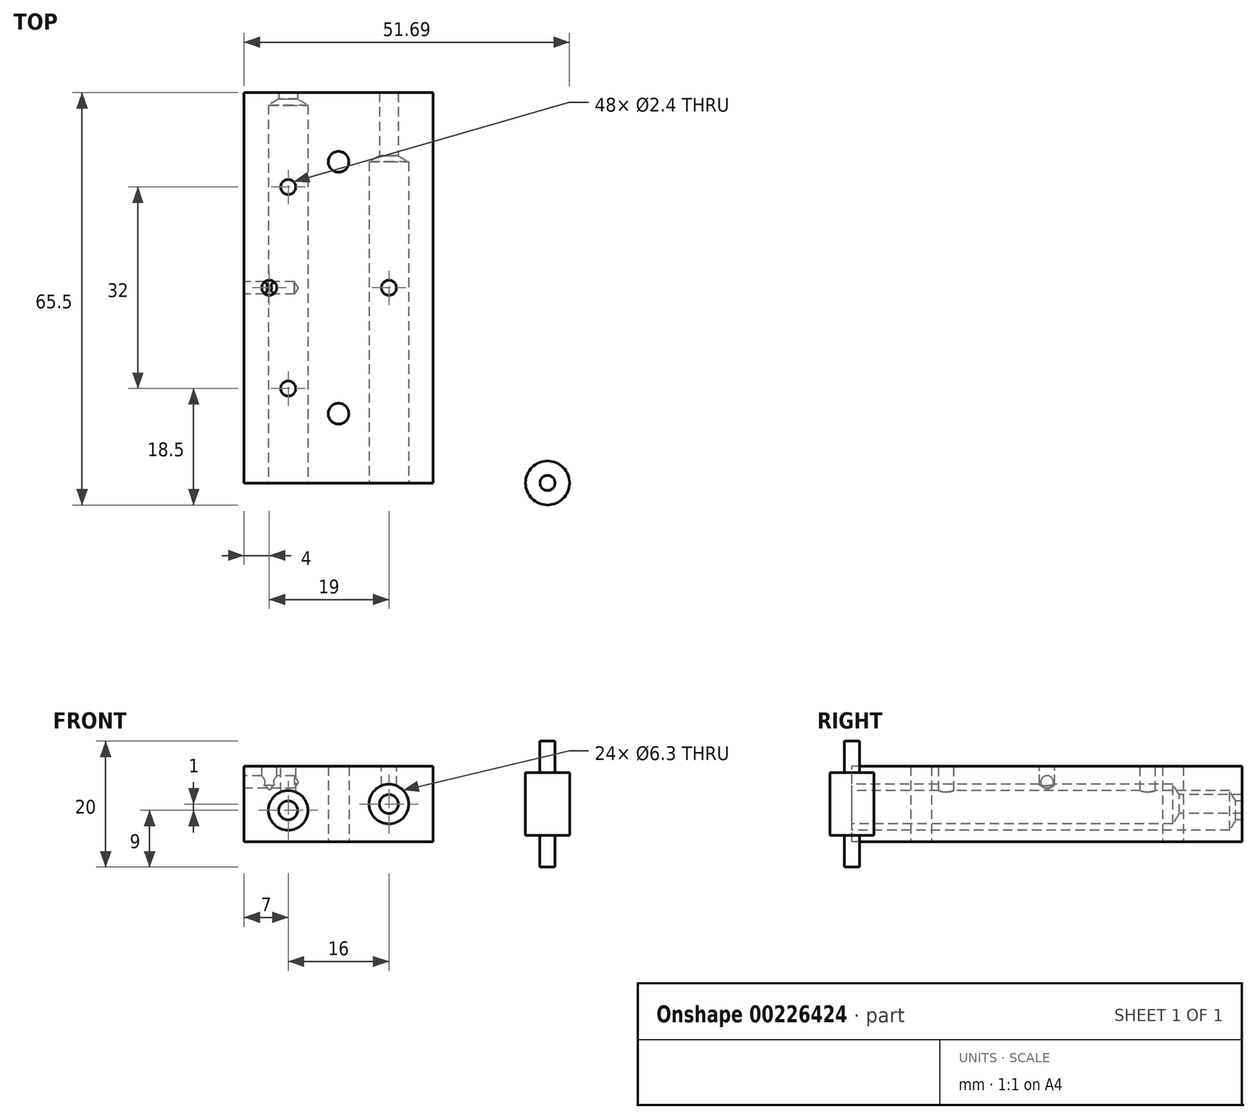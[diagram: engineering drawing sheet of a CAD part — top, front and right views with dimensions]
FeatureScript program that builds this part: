
annotation { "Feature Type Name" : "Feature", "Feature Type Description" : "" }
export const myFeature = defineFeature(function(context is Context, id is Id, definition is map)
    precondition{}
    {
        {
            var Q0;
            Q0=qCreatedBy(makeId("Front.planeOp"),FACE);
            var sketch = newSketch(context, id + "F0", { "sketchPlane" : qUnion([Q0])});
            skLineSegment(sketch, "E0.bottom", {"start": v(15, -6) * mm, "end": v(-15, -6) * mm});
            skLineSegment(sketch, "E0.top", {"start": v(15, 6) * mm, "end": v(-15, 6) * mm});
            skLineSegment(sketch, "E0.left", {"start": v(15, -6) * mm, "end": v(15, 6) * mm});
            skLineSegment(sketch, "E0.right", {"start": v(-15, -6) * mm, "end": v(-15, 6) * mm});
            skPoint(sketch, "E0.middle", {"position": v(0, 0) * mm});
            skPoint(sketch, "E1", {"position": v(-8, -1) * mm});
            skPoint(sketch, "E2", {"position": v(8, 0) * mm});
            skSolve(sketch);
        }
        {
            var Q0;
            Q0=makeQuery(id+"F0.imprint","IMPRINT",FACE,{"disambiguationData":[TD([[makeQuery(id+"F0.imprint","IMPRINT",EDGE,{"derivedFrom":sQuery(id+"F0.wireOp",EDGE,"E0.bottom")}),-1.0]])]});
            extrude(context, id + "F1", {"entities" : qUnion([Q0]), "oppositeDirection" : true, "depth" : 62 * mm});
        }
        {
            var Q0;
            Q0=sQuery(id+"F0.wireOp",VERTEX,"E1");
            var Q1;
            Q1=makeQuery(id+"F1.opExtrude","SWEPT_BODY",BODY,{"disambiguationData":[OSD([sQuery(id+"F0.wireOp",EDGE,"E0.bottom"),sQuery(id+"F0.wireOp",EDGE,"E0.top"),sQuery(id+"F0.wireOp",EDGE,"E0.left"),sQuery(id+"F0.wireOp",EDGE,"E0.right")])]});
            hole(context, id + "F2", {"style" : HoleStyle.SIMPLE, "endStyle" : HoleEndStyle.BLIND, "holeDiameter" : 6.3 * mm, "holeDepth" : 60 * mm, "startFromSketch" : true, "locations" : qUnion([Q0]), "scope" : qUnion([Q1])});
        }
        {
            var Q0;
            Q0=sQuery(id+"F0.wireOp",VERTEX,"E2");
            var Q1;
            Q1=makeQuery(id+"F1.opExtrude","SWEPT_BODY",BODY,{"disambiguationData":[OSD([sQuery(id+"F0.wireOp",EDGE,"E0.bottom"),sQuery(id+"F0.wireOp",EDGE,"E0.top"),sQuery(id+"F0.wireOp",EDGE,"E0.left"),sQuery(id+"F0.wireOp",EDGE,"E0.right")])]});
            hole(context, id + "F3", {"style" : HoleStyle.SIMPLE, "endStyle" : HoleEndStyle.BLIND, "holeDiameter" : 6.3 * mm, "holeDepth" : 51 * mm, "startFromSketch" : true, "locations" : qUnion([Q0]), "scope" : qUnion([Q1])});
        }
        {
            var Q0;
            Q0=makeQuery(id+"F1.opExtrude","SWEPT_FACE",FACE,{"disambiguationData":[OSD([sQuery(id+"F0.wireOp",EDGE,"E0.bottom")])]});
            var sketch = newSketch(context, id + "F4", { "sketchPlane" : qUnion([Q0])});
            skPoint(sketch, "E3", {"position": v(0, -11) * mm});
            skPoint(sketch, "E4", {"position": v(0, -51) * mm});
            skSolve(sketch);
        }
        {
            var Q0;
            Q0=sQuery(id+"F4.wireOp",VERTEX,"E3");
            var Q1;
            Q1=sQuery(id+"F4.wireOp",VERTEX,"E4");
            var Q2;
            Q2=makeQuery(id+"F1.opExtrude","SWEPT_BODY",BODY,{"disambiguationData":[OSD([sQuery(id+"F0.wireOp",EDGE,"E0.bottom"),sQuery(id+"F0.wireOp",EDGE,"E0.top"),sQuery(id+"F0.wireOp",EDGE,"E0.left"),sQuery(id+"F0.wireOp",EDGE,"E0.right")])]});
            hole(context, id + "F5", {"style" : HoleStyle.SIMPLE, "endStyle" : HoleEndStyle.THROUGH, "standardTappedOrClearance" : lookupTablePath({ "standard" : "ISO", "fit" : "Normal", "size" : "M3", "type" : "Clearance" }), "standardBlindInLast" : lookupTablePath({ "fit" : "Standard", "standard" : "ISO", "size" : "M3", "type" : "Clearance" }), "holeDiameter" : 3.3 * mm, "locations" : qUnion([Q0, Q1]), "scope" : qUnion([Q2]), "isTappedThrough" : true});
        }
        {
            var Q0;
            Q0=qCreatedBy(makeId("Top.planeOp"),FACE);
            var sketch = newSketch(context, id + "F6", { "sketchPlane" : qUnion([Q0])});
            skCircle(sketch, "E5", {"center": v(33.2, 0) * mm, "radius": 1.2 * mm});
            skCircle(sketch, "E6", {"center": v(33.2, 0) * mm, "radius": 3.5 * mm});
            skSolve(sketch);
        }
        {
            var Q0;
            Q0=makeQuery(id+"F6.imprint","IMPRINT",FACE,{"disambiguationData":[TD([[makeQuery(id+"F6.imprint","IMPRINT",EDGE,{"derivedFrom":sQuery(id+"F6.wireOp",EDGE,"E5")}),1.0]])]});
            var Q1;
            Q1=sQuery(id+"F6.wireOp",EDGE,"E5");
            extrude(context, id + "F7", {"entities" : qUnion([Q0]), "surfaceEntities" : qUnion([Q1]), "endBound" : BoundingType.SYMMETRIC, "depth" : 20 * mm});
        }
        {
            var Q0;
            Q0 = qSketchRegion(id + "F6", true);
            var Q1;
            Q1 = qSketchRegion(id + "FU8VzBIHLZZ5y2s_1", true);
            extrude(context, id + "F8", {"entities" : qUnion([Q0, Q1]), "operationType" : NewBodyOperationType.ADD, "endBound" : BoundingType.SYMMETRIC, "depth" : 10 * mm});
        }
        {
            var Q0;
            Q0=makeQuery(id+"F1.opExtrude","SWEPT_FACE",FACE,{"disambiguationData":[OSD([sQuery(id+"F0.wireOp",EDGE,"E0.right")])]});
            var sketch = newSketch(context, id + "F9", { "sketchPlane" : qUnion([Q0])});
            skPoint(sketch, "E7", {"position": v(-31, 3.5) * mm});
            skSolve(sketch);
        }
        {
            var Q0;
            Q0=sQuery(id+"F9.wireOp",VERTEX,"E7");
            var Q1;
            Q1=makeQuery(id+"F1.opExtrude","SWEPT_BODY",BODY,{"disambiguationData":[OSD([sQuery(id+"F0.wireOp",EDGE,"E0.bottom"),sQuery(id+"F0.wireOp",EDGE,"E0.top"),sQuery(id+"F0.wireOp",EDGE,"E0.left"),sQuery(id+"F0.wireOp",EDGE,"E0.right")])]});
            hole(context, id + "F10", {"style" : HoleStyle.SIMPLE, "endStyle" : HoleEndStyle.BLIND, "holeDiameter" : 2 * mm, "holeDepth" : 8 * mm, "startFromSketch" : true, "locations" : qUnion([Q0]), "scope" : qUnion([Q1])});
        }
        {
            var Q0;
            Q0=makeQuery(id+"F1.opExtrude","SWEPT_FACE",FACE,{"disambiguationData":[OSD([sQuery(id+"F0.wireOp",EDGE,"E0.top")])]});
            var sketch = newSketch(context, id + "F11", { "sketchPlane" : qUnion([Q0])});
            skPoint(sketch, "E8", {"position": v(-8, 15) * mm});
            skPoint(sketch, "E9", {"position": v(-11, 31) * mm});
            skPoint(sketch, "E9.positionSnap0", {"position": v(-15, 31) * mm});
            skPoint(sketch, "E10", {"position": v(8, 31) * mm});
            skPoint(sketch, "E11", {"position": v(-8, 47) * mm});
            skSolve(sketch);
        }
        {
            var Q0;
            Q0=sQuery(id+"F11.wireOp",VERTEX,"E8");
            var Q1;
            Q1=sQuery(id+"F11.wireOp",VERTEX,"E11");
            var Q2;
            Q2=sQuery(id+"F11.wireOp",VERTEX,"E10");
            var Q3;
            Q3=makeQuery(id+"F1.opExtrude","SWEPT_BODY",BODY,{"disambiguationData":[OSD([sQuery(id+"F0.wireOp",EDGE,"E0.bottom"),sQuery(id+"F0.wireOp",EDGE,"E0.top"),sQuery(id+"F0.wireOp",EDGE,"E0.left"),sQuery(id+"F0.wireOp",EDGE,"E0.right")])]});
            hole(context, id + "F12", {"style" : HoleStyle.SIMPLE, "endStyle" : HoleEndStyle.BLIND, "standardTappedOrClearance" : lookupTablePath({ "standard" : "ISO", "engagement" : "75%", "pitch" : "0.6 mm", "size" : "M3", "type" : "Tapped" }), "standardBlindInLast" : lookupTablePath({ "standard" : "ISO", "engagement" : "75%", "pitch" : "0.6 mm", "size" : "M3", "type" : "Tapped" }), "holeDiameter" : 2.4 * mm, "holeDepth" : 8 * mm, "startFromSketch" : true, "locations" : qUnion([Q0, Q1, Q2]), "scope" : qUnion([Q3])});
        }
        {
            var Q0;
            Q0=sQuery(id+"F11.wireOp",VERTEX,"E9");
            var Q1;
            Q1=makeQuery(id+"F1.opExtrude","SWEPT_BODY",BODY,{"disambiguationData":[OSD([sQuery(id+"F0.wireOp",EDGE,"E0.bottom"),sQuery(id+"F0.wireOp",EDGE,"E0.top"),sQuery(id+"F0.wireOp",EDGE,"E0.left"),sQuery(id+"F0.wireOp",EDGE,"E0.right")])]});
            hole(context, id + "F13", {"style" : HoleStyle.SIMPLE, "endStyle" : HoleEndStyle.BLIND, "standardTappedOrClearance" : lookupTablePath({ "standard" : "ISO", "engagement" : "75%", "pitch" : "0.6 mm", "size" : "M3", "type" : "Tapped" }), "standardBlindInLast" : lookupTablePath({ "standard" : "ISO", "engagement" : "75%", "pitch" : "0.6 mm", "size" : "M3", "type" : "Tapped" }), "holeDiameter" : 2.4 * mm, "holeDepth" : 3 * mm, "startFromSketch" : true, "locations" : qUnion([Q0]), "scope" : qUnion([Q1])});
        }
        {
            var Q0;
            Q0=sQuery(id+"F0.wireOp",VERTEX,"E1");
            var Q1;
            Q1=sQuery(id+"F0.wireOp",VERTEX,"E2");
            var Q2;
            Q2=makeQuery(id+"F1.opExtrude","SWEPT_BODY",BODY,{"disambiguationData":[OSD([sQuery(id+"F0.wireOp",EDGE,"E0.bottom"),sQuery(id+"F0.wireOp",EDGE,"E0.top"),sQuery(id+"F0.wireOp",EDGE,"E0.left"),sQuery(id+"F0.wireOp",EDGE,"E0.right")])]});
            hole(context, id + "F14", {"style" : HoleStyle.SIMPLE, "endStyle" : HoleEndStyle.THROUGH, "holeDiameter" : 3 * mm, "startFromSketch" : true, "locations" : qUnion([Q0, Q1]), "scope" : qUnion([Q2]), "isTappedThrough" : true});
        }
    });
